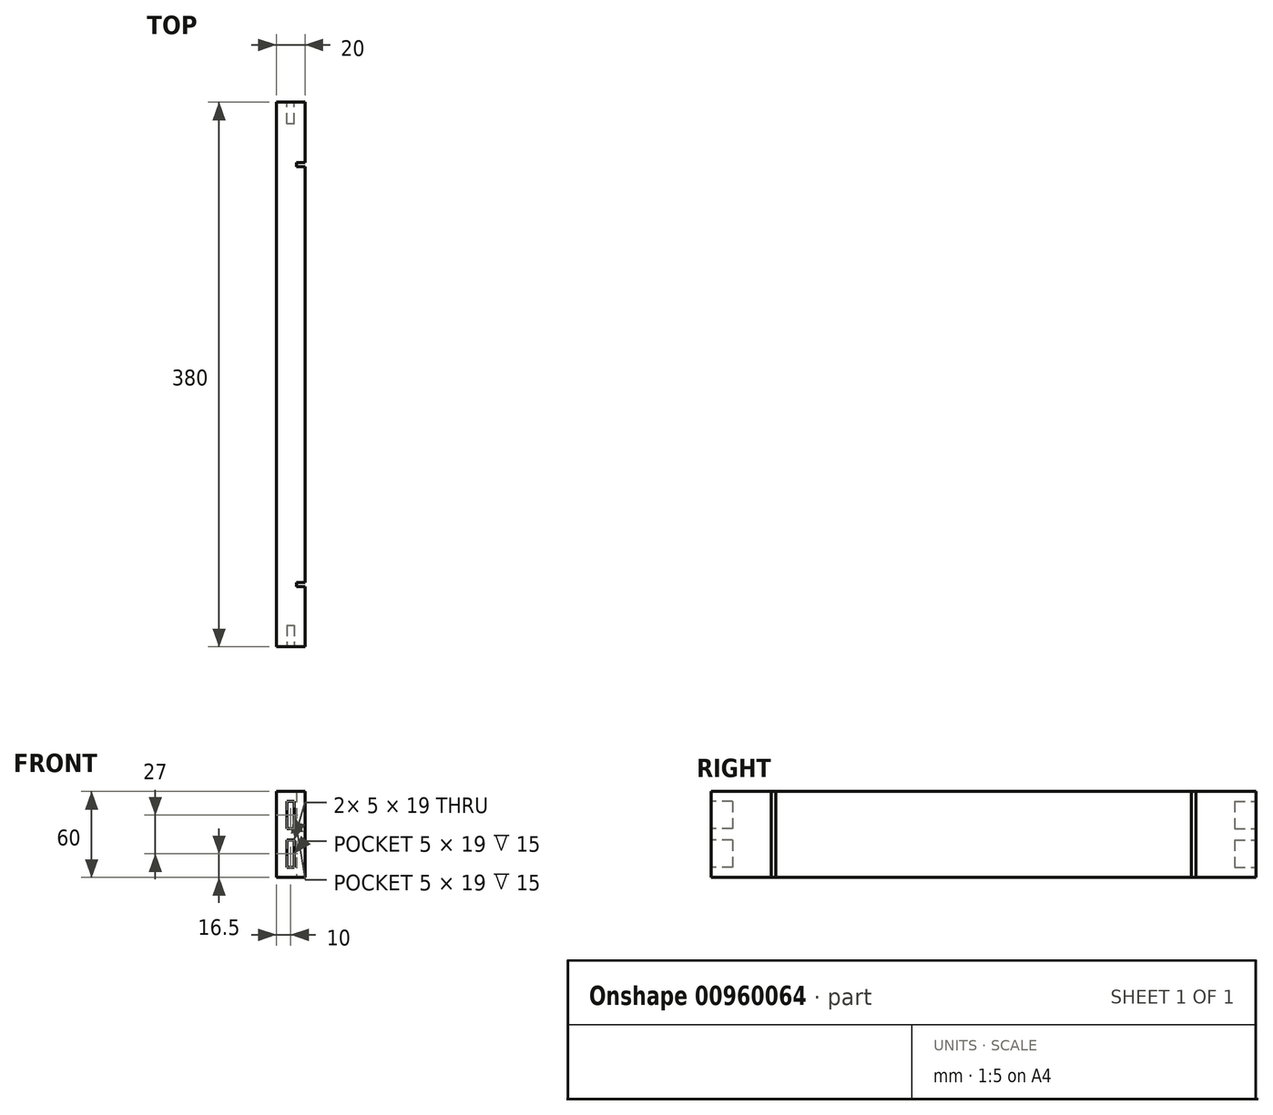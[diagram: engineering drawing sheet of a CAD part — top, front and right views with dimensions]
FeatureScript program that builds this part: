
annotation { "Feature Type Name" : "Feature", "Feature Type Description" : "" }
export const myFeature = defineFeature(function(context is Context, id is Id, definition is map)
    precondition{}
    {
        {
            var Q0;
            Q0=qCreatedBy(makeId("Right.planeOp"),FACE);
            var sketch = newSketch(context, id + "F0", { "sketchPlane" : qUnion([Q0])});
            skLineSegment(sketch, "E0", {"start": v(-190, 0) * mm, "end": v(-190, -60) * mm});
            skLineSegment(sketch, "E1", {"start": v(-190, -60) * mm, "end": v(0, -60) * mm});
            skLineSegment(sketch, "E2.MirrorCS", {"start": v(190, 0) * mm, "end": v(190, -60) * mm});
            skLineSegment(sketch, "E3.MirrorCS", {"start": v(190, -60) * mm, "end": v(0, -60) * mm});
            skLineSegment(sketch, "E4", {"start": v(-190, 0) * mm, "end": v(190, 0) * mm});
            skSolve(sketch);
        }
        {
            var Q0;
            Q0=makeQuery(id+"F0.imprint","IMPRINT",FACE,{"disambiguationData":[TD([[makeQuery(id+"F0.imprint","IMPRINT",EDGE,{"derivedFrom":sQuery(id+"F0.wireOp",EDGE,"CwsxdDG5-br4k-XFxC-YtaJ-n2vhq56D0rb5")}),1.0]])]});
            var Q1;
            Q1=makeQuery(id+"F0.imprint","IMPRINT",FACE,{"disambiguationData":[TD([[makeQuery(id+"F0.imprint","IMPRINT",EDGE,{"derivedFrom":sQuery(id+"F0.wireOp",EDGE,"E0")}),1.0]])]});
            extrude(context, id + "F1", {"entities" : qUnion([Q0, Q1]), "depth" : 20 * mm, "offsetDistance" : 25 * mm});
        }
        {
            var Q0;
            Q0=makeQuery(id+"F1.opExtrude","SWEPT_FACE",FACE,{"disambiguationData":[OSD([sQuery(id+"F0.wireOp",EDGE,"E1"),sQuery(id+"F0.wireOp",EDGE,"E3.MirrorCS")])]});
            var sketch = newSketch(context, id + "F2", { "sketchPlane" : qUnion([Q0])});
            skLineSegment(sketch, "E5.bottom", {"start": v(20, 148) * mm, "end": v(14, 148) * mm});
            skLineSegment(sketch, "E5.top", {"start": v(20, 145) * mm, "end": v(14, 145) * mm});
            skLineSegment(sketch, "E5.left", {"start": v(20, 148) * mm, "end": v(20, 145) * mm});
            skLineSegment(sketch, "E5.right", {"start": v(14, 148) * mm, "end": v(14, 145) * mm});
            skLineSegment(sketch, "E6.bottom", {"start": v(20, -148) * mm, "end": v(14, -148) * mm});
            skLineSegment(sketch, "E6.top", {"start": v(20, -145) * mm, "end": v(14, -145) * mm});
            skLineSegment(sketch, "E6.left", {"start": v(20, -148) * mm, "end": v(20, -145) * mm});
            skLineSegment(sketch, "E6.right", {"start": v(14, -148) * mm, "end": v(14, -145) * mm});
            skSolve(sketch);
        }
        {
            var Q0;
            Q0=makeQuery(id+"F2.imprint","IMPRINT",FACE,{"disambiguationData":[TD([[makeQuery(id+"F2.imprint","IMPRINT",EDGE,{"derivedFrom":sQuery(id+"F2.wireOp",EDGE,"E5.bottom")}),1.0]])]});
            var Q1;
            Q1=makeQuery(id+"F2.imprint","IMPRINT",FACE,{"disambiguationData":[TD([[makeQuery(id+"F2.imprint","IMPRINT",EDGE,{"derivedFrom":sQuery(id+"F2.wireOp",EDGE,"E6.bottom")}),-1.0]])]});
            extrude(context, id + "F3", {"entities" : qUnion([Q0, Q1]), "operationType" : NewBodyOperationType.REMOVE, "oppositeDirection" : true, "depth" : 60 * mm, "offsetDistance" : 25 * mm});
        }
        {
            var Q0;
            Q0=makeQuery(id+"F1.opExtrude","SWEPT_FACE",FACE,{"disambiguationData":[OSD([sQuery(id+"F0.wireOp",EDGE,"E0")])]});
            var sketch = newSketch(context, id + "F4", { "sketchPlane" : qUnion([Q0])});
            skPoint(sketch, "E7.middle", {"position": v(10, -30) * mm});
            skPoint(sketch, "E7.middle.positionSnap0", {"position": v(0, -30) * mm});
            skPoint(sketch, "E7.middle.positionSnap1", {"position": v(10, 0) * mm});
            skPoint(sketch, "E7.centerSnap0", {"position": v(0, -30) * mm});
            skPoint(sketch, "E7.centerSnap1", {"position": v(10, 0) * mm});
            skLineSegment(sketch, "E8.bottom", {"start": v(7.5, -7) * mm, "end": v(12.5, -7) * mm});
            skLineSegment(sketch, "E8.top", {"start": v(7.5, -26) * mm, "end": v(12.5, -26) * mm});
            skLineSegment(sketch, "E8.left", {"start": v(7.5, -7) * mm, "end": v(7.5, -26) * mm});
            skLineSegment(sketch, "E8.right", {"start": v(12.5, -7) * mm, "end": v(12.5, -26) * mm});
            skLineSegment(sketch, "E9.bottom", {"start": v(7.5, -34) * mm, "end": v(12.5, -34) * mm});
            skLineSegment(sketch, "E9.top", {"start": v(7.5, -53) * mm, "end": v(12.5, -53) * mm});
            skLineSegment(sketch, "E9.left", {"start": v(7.5, -34) * mm, "end": v(7.5, -53) * mm});
            skLineSegment(sketch, "E9.right", {"start": v(12.5, -34) * mm, "end": v(12.5, -53) * mm});
            skSolve(sketch);
        }
        {
            var Q0;
            Q0=makeQuery(id+"F4.imprint","IMPRINT",FACE,{"disambiguationData":[TD([[makeQuery(id+"F4.imprint","IMPRINT",EDGE,{"derivedFrom":sQuery(id+"F4.wireOp",EDGE,"E8.bottom")}),-1.0]])]});
            var Q1;
            Q1=makeQuery(id+"F4.imprint","IMPRINT",FACE,{"disambiguationData":[TD([[makeQuery(id+"F4.imprint","IMPRINT",EDGE,{"derivedFrom":sQuery(id+"F4.wireOp",EDGE,"E9.bottom")}),-1.0]])]});
            extrude(context, id + "F5", {"entities" : qUnion([Q0, Q1]), "operationType" : NewBodyOperationType.REMOVE, "oppositeDirection" : true, "depth" : 15 * mm, "offsetDistance" : 25 * mm});
        }
        {
            var Q0;
            Q0=makeQuery(id+"F1.opExtrude","SWEPT_FACE",FACE,{"disambiguationData":[OSD([sQuery(id+"F0.wireOp",EDGE,"E2.MirrorCS")])]});
            var sketch = newSketch(context, id + "F6", { "sketchPlane" : qUnion([Q0])});
            skLineSegment(sketch, "E10.bottom", {"start": v(-12.5, -7) * mm, "end": v(-7.5, -7) * mm});
            skLineSegment(sketch, "E10.top", {"start": v(-12.5, -26) * mm, "end": v(-7.5, -26) * mm});
            skLineSegment(sketch, "E10.left", {"start": v(-12.5, -7) * mm, "end": v(-12.5, -26) * mm});
            skLineSegment(sketch, "E10.right", {"start": v(-7.5, -7) * mm, "end": v(-7.5, -26) * mm});
            skLineSegment(sketch, "E11.bottom", {"start": v(-12.5, -34) * mm, "end": v(-7.5, -34) * mm});
            skLineSegment(sketch, "E11.top", {"start": v(-12.5, -53) * mm, "end": v(-7.5, -53) * mm});
            skLineSegment(sketch, "E11.left", {"start": v(-12.5, -34) * mm, "end": v(-12.5, -53) * mm});
            skLineSegment(sketch, "E11.right", {"start": v(-7.5, -34) * mm, "end": v(-7.5, -53) * mm});
            skSolve(sketch);
        }
        {
            var Q0;
            Q0=makeQuery(id+"F6.imprint","IMPRINT",FACE,{"disambiguationData":[TD([[makeQuery(id+"F6.imprint","IMPRINT",EDGE,{"derivedFrom":sQuery(id+"F6.wireOp",EDGE,"E10.bottom")}),-1.0]])]});
            var Q1;
            Q1=makeQuery(id+"F6.imprint","IMPRINT",FACE,{"disambiguationData":[TD([[makeQuery(id+"F6.imprint","IMPRINT",EDGE,{"derivedFrom":sQuery(id+"F6.wireOp",EDGE,"E11.bottom")}),-1.0]])]});
            extrude(context, id + "F7", {"entities" : qUnion([Q0, Q1]), "operationType" : NewBodyOperationType.REMOVE, "oppositeDirection" : true, "depth" : 15 * mm, "offsetDistance" : 25 * mm});
        }
    });
